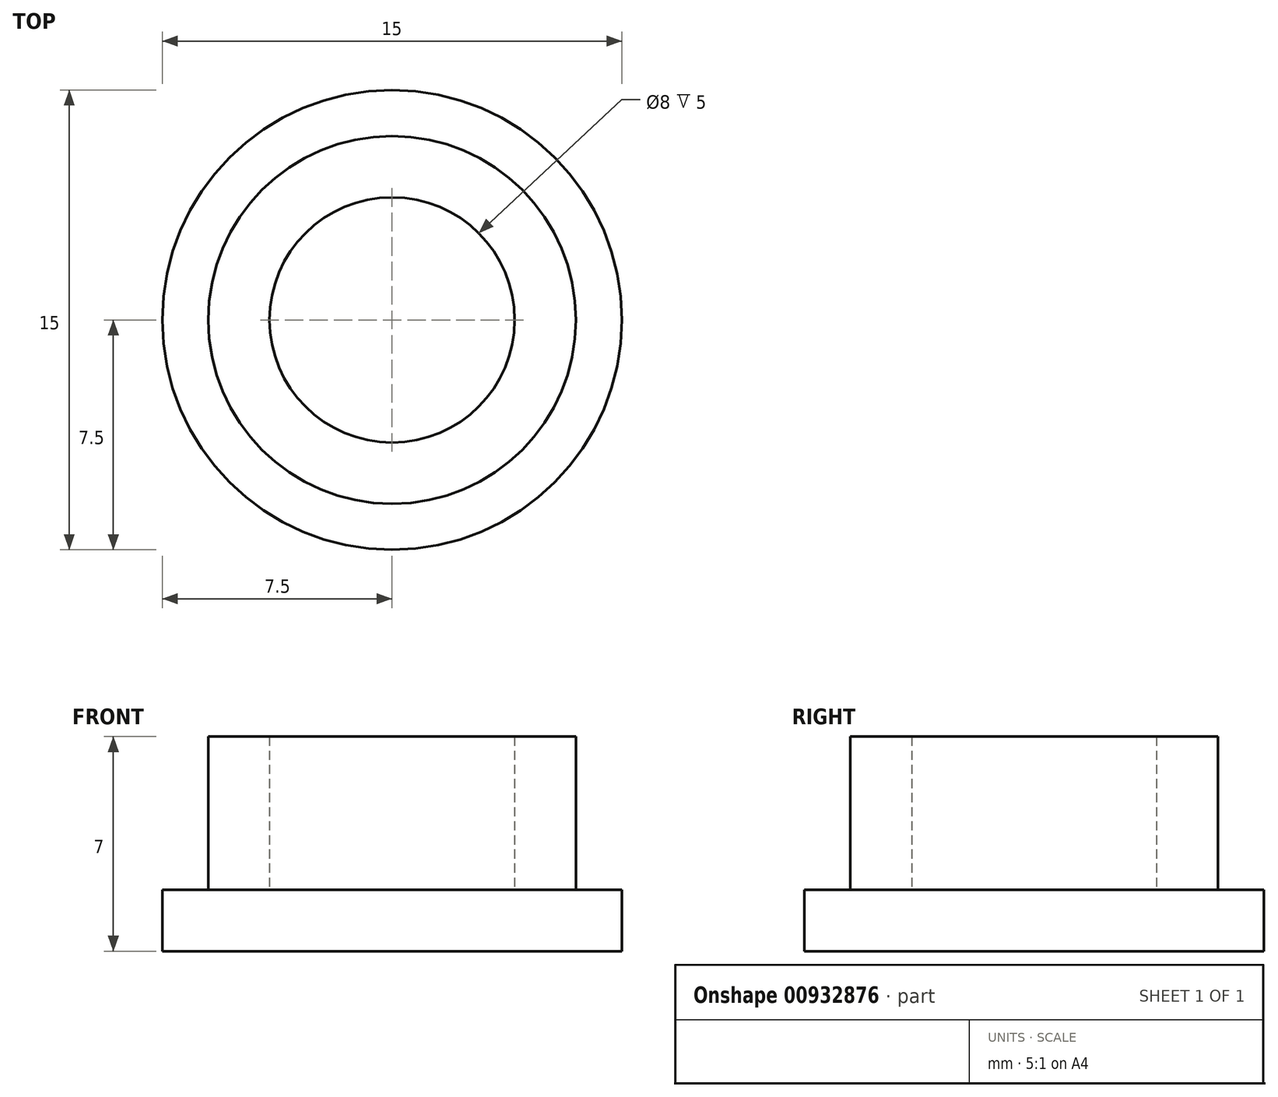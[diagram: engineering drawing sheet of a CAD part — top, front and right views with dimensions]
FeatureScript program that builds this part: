
annotation { "Feature Type Name" : "Feature", "Feature Type Description" : "" }
export const myFeature = defineFeature(function(context is Context, id is Id, definition is map)
    precondition{}
    {
        {
            var Q0;
            Q0=qCreatedBy(makeId("Top.planeOp"),FACE);
            var sketch = newSketch(context, id + "F0", { "sketchPlane" : qUnion([Q0])});
            skCircle(sketch, "E0", {"center": v(0, 0) * mm, "radius": 7.5 * mm});
            skSolve(sketch);
        }
        {
            var Q0;
            Q0 = qSketchRegion(id + "F0", true);
            extrude(context, id + "F1", {"entities" : qUnion([Q0]), "depth" : 2 * mm, "offsetDistance" : 25 * mm});
        }
        {
            var Q0;
            Q0=makeQuery(id+"F1.opExtrude","CAP_FACE",FACE,{"disambiguationData":[OSD([sQuery(id+"F0.wireOp",EDGE,"E0")])],"isStart":false});
            var sketch = newSketch(context, id + "F2", { "sketchPlane" : qUnion([Q0])});
            skCircle(sketch, "E1", {"center": v(0, 0) * mm, "radius": 6 * mm});
            skSolve(sketch);
        }
        {
            var Q0;
            Q0 = qSketchRegion(id + "F2", true);
            extrude(context, id + "F3", {"entities" : qUnion([Q0]), "operationType" : NewBodyOperationType.ADD, "depth" : 5 * mm, "offsetDistance" : 25 * mm});
        }
        {
            var Q0;
            Q0=makeQuery(id+"F3.opExtrude","CAP_FACE",FACE,{"disambiguationData":[OSD([sQuery(id+"F2.wireOp",EDGE,"E1")])],"isStart":false});
            shell(context, id + "F4", {"entities" : qUnion([Q0]), "thickness" : 2 * mm});
        }
    });
